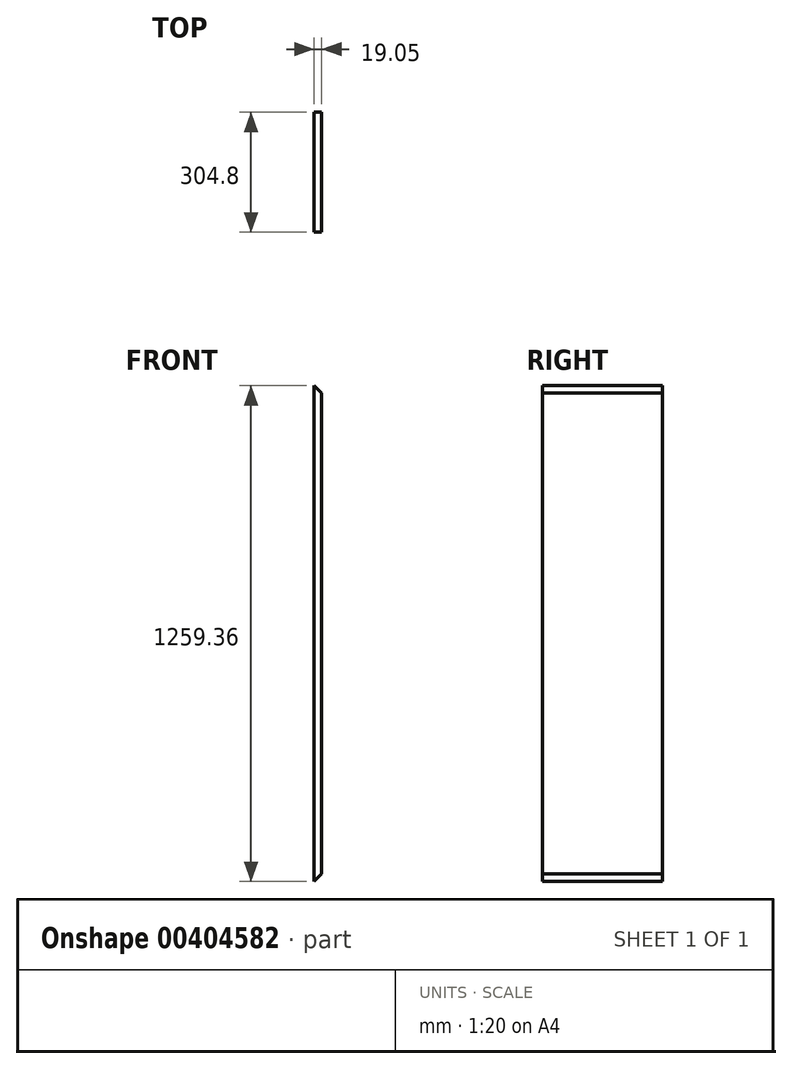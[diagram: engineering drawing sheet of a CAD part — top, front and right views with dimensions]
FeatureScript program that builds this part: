
annotation { "Feature Type Name" : "Feature", "Feature Type Description" : "" }
export const myFeature = defineFeature(function(context is Context, id is Id, definition is map)
    precondition{}
    {
        {
            var Q0;
            Q0=qCreatedBy(makeId("Front.planeOp"),FACE);
            var sketch = newSketch(context, id + "F0", { "sketchPlane" : qUnion([Q0])});
            skLineSegment(sketch, "E0.left", {"start": v(0, -629.68) * mm, "end": v(0, 629.68) * mm});
            skLineSegment(sketch, "E0.right", {"start": v(19.05, -610.63) * mm, "end": v(19.05, 610.63) * mm});
            skLineSegment(sketch, "E1", {"start": v(0, 629.68) * mm, "end": v(19.05, 610.63) * mm});
            skLineSegment(sketch, "E2", {"start": v(0, -629.68) * mm, "end": v(19.05, -610.63) * mm});
            skSolve(sketch);
        }
        {
            var Q0;
            Q0 = qSketchRegion(id + "F0", true);
            extrude(context, id + "F1", {"entities" : qUnion([Q0]), "endBound" : BoundingType.SYMMETRIC, "depth" : 304.8 * mm});
        }
    });
